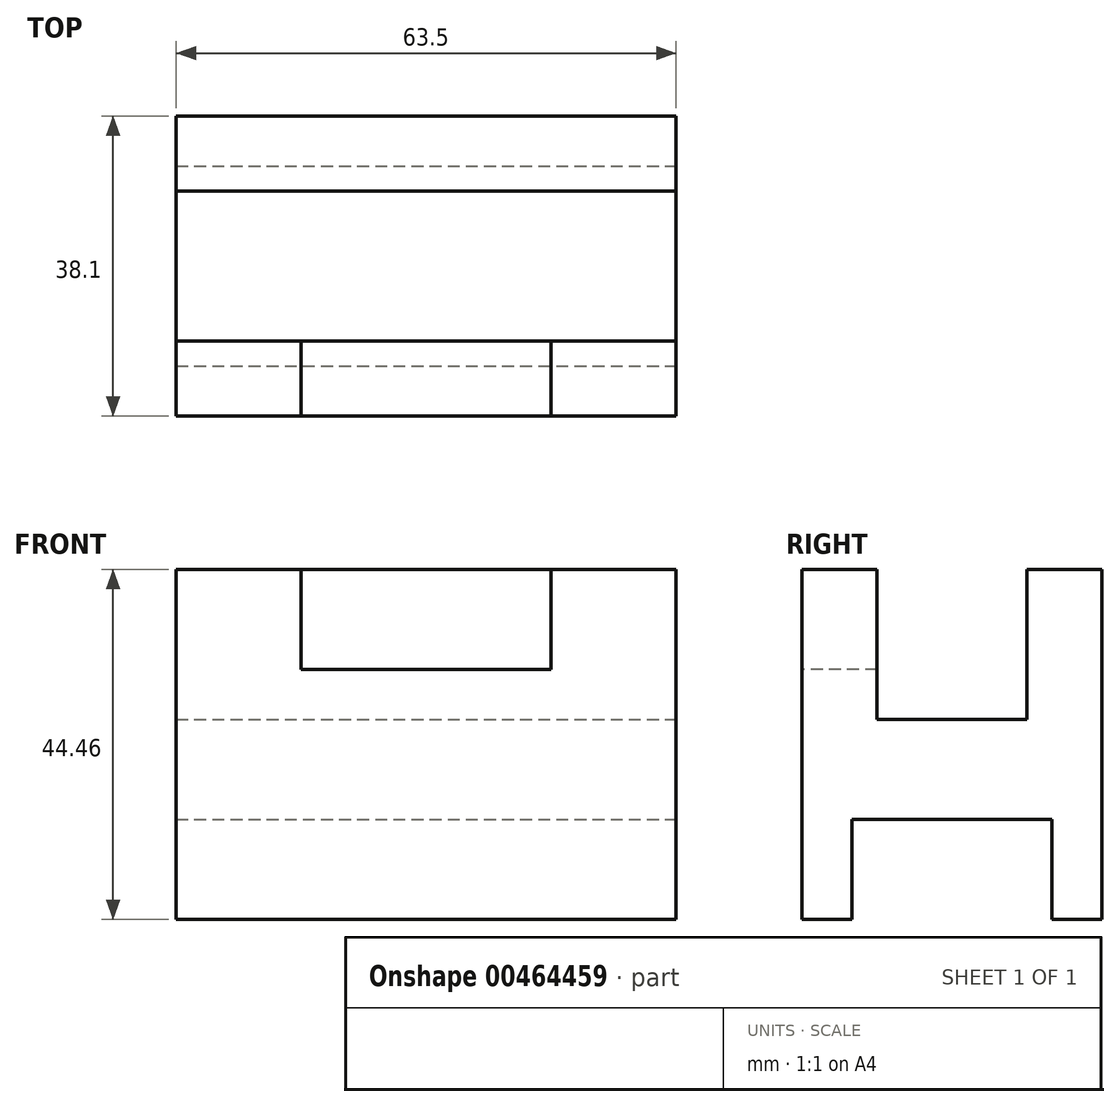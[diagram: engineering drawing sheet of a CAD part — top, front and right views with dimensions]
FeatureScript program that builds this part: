
annotation { "Feature Type Name" : "Feature", "Feature Type Description" : "" }
export const myFeature = defineFeature(function(context is Context, id is Id, definition is map)
    precondition{}
    {
        {
            var Q0;
            Q0=qCreatedBy(makeId("Front.planeOp"),FACE);
            var sketch = newSketch(context, id + "F0", { "sketchPlane" : qUnion([Q0])});
            skLineSegment(sketch, "E0.bottom", {"start": v(31.75, 22.23) * mm, "end": v(-31.75, 22.23) * mm});
            skLineSegment(sketch, "E0.top", {"start": v(31.75, -22.23) * mm, "end": v(-31.75, -22.23) * mm});
            skLineSegment(sketch, "E0.left", {"start": v(31.75, 22.23) * mm, "end": v(31.75, -22.23) * mm});
            skLineSegment(sketch, "E0.right", {"start": v(-31.75, 22.23) * mm, "end": v(-31.75, -22.23) * mm});
            skPoint(sketch, "E0.middle", {"position": v(0, 0) * mm});
            skSolve(sketch);
        }
        {
            var Q0;
            Q0=makeQuery(id+"F0.imprint","IMPRINT",FACE,{"disambiguationData":[TD([[makeQuery(id+"F0.imprint","IMPRINT",EDGE,{"derivedFrom":sQuery(id+"F0.wireOp",EDGE,"E0.bottom")}),1.0]])]});
            extrude(context, id + "F1", {"entities" : qUnion([Q0]), "depth" : 38.1 * mm});
        }
        {
            var Q0;
            Q0=makeQuery(id+"F1.opExtrude","CAP_FACE",FACE,{"disambiguationData":[OSD([sQuery(id+"F0.wireOp",EDGE,"E0.bottom"),sQuery(id+"F0.wireOp",EDGE,"E0.top"),sQuery(id+"F0.wireOp",EDGE,"E0.left"),sQuery(id+"F0.wireOp",EDGE,"E0.right")])],"isStart":false});
            var sketch = newSketch(context, id + "F2", { "sketchPlane" : qUnion([Q0])});
            skLineSegment(sketch, "E1.bottom", {"start": v(-15.88, 22.23) * mm, "end": v(15.87, 22.23) * mm});
            skLineSegment(sketch, "E1.top", {"start": v(-15.88, 9.53) * mm, "end": v(15.87, 9.53) * mm});
            skLineSegment(sketch, "E1.left", {"start": v(-15.88, 22.23) * mm, "end": v(-15.88, 9.53) * mm});
            skLineSegment(sketch, "E1.right", {"start": v(15.87, 22.23) * mm, "end": v(15.87, 9.52) * mm});
            skSolve(sketch);
        }
        {
            var Q0;
            Q0 = qSketchRegion(id + "F2", true);
            extrude(context, id + "F3", {"entities" : qUnion([Q0]), "operationType" : NewBodyOperationType.REMOVE, "oppositeDirection" : true, "depth" : 9.52 * mm});
        }
        {
            var Q0;
            Q0=makeQuery(id+"F1.opExtrude","SWEPT_FACE",FACE,{"disambiguationData":[OSD([sQuery(id+"F0.wireOp",EDGE,"E0.left")])]});
            var sketch = newSketch(context, id + "F4", { "sketchPlane" : qUnion([Q0])});
            skLineSegment(sketch, "E2.bottom", {"start": v(-28.58, 22.22) * mm, "end": v(-9.53, 22.22) * mm});
            skLineSegment(sketch, "E2.top", {"start": v(-28.58, 3.17) * mm, "end": v(-9.53, 3.17) * mm});
            skLineSegment(sketch, "E2.left", {"start": v(-28.58, 22.22) * mm, "end": v(-28.58, 3.17) * mm});
            skLineSegment(sketch, "E2.right", {"start": v(-9.53, 22.22) * mm, "end": v(-9.53, 3.18) * mm});
            skSolve(sketch);
        }
        {
            var Q0;
            Q0 = qSketchRegion(id + "F4", true);
            extrude(context, id + "F5", {"entities" : qUnion([Q0]), "operationType" : NewBodyOperationType.REMOVE, "endBound" : BoundingType.THROUGH_ALL, "oppositeDirection" : true, "depth" : 25.4 * mm});
        }
        {
            var Q0;
            Q0=makeQuery(id+"F1.opExtrude","SWEPT_FACE",FACE,{"disambiguationData":[OSD([sQuery(id+"F0.wireOp",EDGE,"E0.left")])]});
            var sketch = newSketch(context, id + "F6", { "sketchPlane" : qUnion([Q0])});
            skLineSegment(sketch, "E3.bottom", {"start": v(-31.75, -22.23) * mm, "end": v(-6.35, -22.23) * mm});
            skLineSegment(sketch, "E3.top", {"start": v(-31.75, -9.53) * mm, "end": v(-6.35, -9.53) * mm});
            skLineSegment(sketch, "E3.left", {"start": v(-31.75, -22.23) * mm, "end": v(-31.75, -9.53) * mm});
            skLineSegment(sketch, "E3.right", {"start": v(-6.35, -22.23) * mm, "end": v(-6.35, -9.53) * mm});
            skSolve(sketch);
        }
        {
            var Q0;
            Q0 = qSketchRegion(id + "F6", true);
            extrude(context, id + "F7", {"entities" : qUnion([Q0]), "operationType" : NewBodyOperationType.REMOVE, "endBound" : BoundingType.THROUGH_ALL, "oppositeDirection" : true, "depth" : 25.4 * mm});
        }
    });
